# Revit family: Techlam Standard Profile-112mm
name_source: partatom
category: Profiles
revit_build: Autodesk Revit 2016 (Build: 20150220_1215(x64)
units: mm (PartAtom-declared; Revit-internal decimal feet)

## family parameters
Profile Usage = <Generic>
Rotate with component = No

## types (21) — shared parameters
Width = 112 mm  [stored 0.367454 ft]

## per-type parameters (varying)
| type | Depth |
| 88 x 112 | 88 mm  [stored 0.288714 ft] |
| 135 x 112 | 135 mm  [stored 0.442913 ft] |
| 140 x 112 | 140 mm  [stored 0.459318 ft] |
| 180 x 112 | 180 mm  [stored 0.590551 ft] |
| 190 x 112 | 190 mm |
| 225 x 112 | 225 mm  [stored 0.738189 ft] |
| 240 x 112 | 240 mm  [stored 0.787402 ft] |
| 270 x 112 | 270 mm  [stored 0.885827 ft] |
| 290 x 112 | 290 mm  [stored 0.951444 ft] |
| 315 x 112 | 315 mm  [stored 1.03346 ft] |
| 360 x 112 | 360 mm  [stored 1.1811 ft] |
| 405 x 112 | 405 mm  [stored 1.32874 ft] |
| 450 x 112 | 450 mm  [stored 1.47638 ft] |
| 495 x 112 | 495 mm  [stored 1.62402 ft] |
| 540 x 112 | 540 mm  [stored 1.77165 ft] |
| 585 x 112 | 585 mm  [stored 1.91929 ft] |
| 630 x 112 | 630 mm  [stored 2.06693 ft] |
| 675 x 112 | 675 mm  [stored 2.21457 ft] |
| 720 x 112 | 720 mm  [stored 2.3622 ft] |
| 765 x 112 | 765 mm  [stored 2.50984 ft] |
| 810 x 112 | 810 mm |

note: [stored X ft] marks values corroborated as IEEE doubles in the binary element streams (Revit-internal decimal feet)

## geometry (parser evidence)
native form markers: Sweep x1
no freeform markers — native parametric forms only
